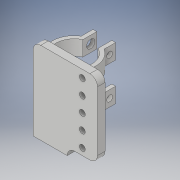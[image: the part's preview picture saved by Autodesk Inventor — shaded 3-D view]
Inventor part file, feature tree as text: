
AUTODESK INVENTOR PART (.ipt)
format: ipt  version: 2018 (Build 220112000, 112)  size: 310,272 bytes
history: native  units: in
note: dims shown in document units (in); Inventor stores cm internally (conversion verified against a paired STEP export)
features: extrude x8, sketch x7, fillet x4, plane x2, pattern_linear x1, mirror x1
ambient origin geometry x8: Origin, YZ Plane, XZ Plane, XY Plane, X Axis, Y Axis, Z Axis, Center Point
bodies: Solid1 (feature_tree)
feature tree (23):
  extrude  "Extrusion1"  Depth=1.0in TaperAngle=0.0deg
  plane  "Work Plane1"
  extrude  "Extrusion2"  Depth=0.5in
  extrude  "Extrusion3"  Depth=0.0984in
  extrude  "Extrusion4"  Depth=0.0787in TaperAngle=0.0deg
  plane  "Work Plane2"
  extrude  "Extrusion5"  Depth=0.25in TaperAngle=0.0deg
  pattern_linear  "Rectangular Pattern1"  Spacing1=0.5625in  [1 undecoded]
  extrude  "Extrusion6"  Depth=0.25in
  extrude  "Extrusion7"  Depth=1.125in
  fillet  "Fillet1"  Radius=2.471in
  extrude  "Extrusion8"  [1 undecoded]
  fillet  "Fillet2"  Radius=0.6729in
  fillet  "Fillet3"  Radius=0.7573in
  fillet  "Fillet4"  Radius=0.1875in
  mirror  "Mirror1"
  sketch  "Sketch1"  dims[d0=1.0in d1=1.0in d2=0.0in]
  sketch  "Sketch3"  dims[d3=0.5in d8=0.0945in]
  sketch  "Sketch4"  dims[d9=0.1969in d10=0.0984in]
  sketch  "Sketch6"  dims[d11=0.0945in d12=0.0787in d13=0.0in]
  sketch  "Sketch7"  dims[d14=0.25in d15=0.25in d16=0.0in]
  sketch  "Sketch8"  dims[d17=1.125in]
  sketch  "Sketch9"  dims[d18=0.5625in d19=0.5625in d20=0.0625in d21=1.125in d23=2.471in d24=0.0in d25=-0.75in d26=1.19in d27=0.125in d28=0.375in d29=1.0in d30=0.125in d31=0.6729in d32=0.7573in d33=0.1875in d34=0.1856in d35=0.3106in d36=0.425in d37=0.55in d38=0.5in d39=0.0in d40=0.7874in d42=1.25in d43=0.194in d44=0.194in d45=0.25in d46=0.25in d47=0.2in d48=0.2in d49=0.5in d50=0.0in d51=0.274in d52=0.274in d53=0.5in d54=0.0in d55=0.2in d56=0.1935in d57=0.5in d59=0.5in d60=0.5in d61=0.5in d64=0.1935in d65=0.1935in d66=0.1935in d67=0.1935in d71=0.25in d72=0.0in d75=0.5in d76=0.25in d77=0.5in d78=0.5in d79=0.5in d80=0.5in d81=0.25in d82=0.25in d83=0.25in]
note: 2 required parameter values undecoded (feature->parameter linkage not recoverable at this tier; creation-order binding heuristic only, values carry confidence <= 0.55)
